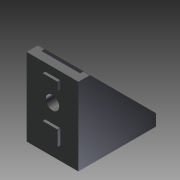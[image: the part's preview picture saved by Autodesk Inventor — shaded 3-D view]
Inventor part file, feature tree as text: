
AUTODESK INVENTOR PART (.ipt)
format: ipt  version: 2016 (Build 200138000, 138)  size: 183,808 bytes
history: native  units: mm
features: other x42, sketch x8, extrude x5, hole x3
ambient origin geometry x8: Origin, YZ Plane, XZ Plane, XY Plane, X Axis, Y Axis, Z Axis, Center Point
bodies: Solid1 (feature_tree)
feature tree (58):
  extrude  "Extrusion1"  Depth=15.0mm TaperAngle=0.0deg
  extrude  "Extrusion2"  Depth=1.0mm TaperAngle=0.0deg
  extrude  "Extrusion3"  TaperAngle=0.0deg  [1 undecoded]
  hole  "Hole1"  [1 undecoded]
  hole  "Hole2"  [1 undecoded]
  hole  "Hole3"  [1 undecoded]
  extrude  "Extrusion4"  [1 undecoded]
  extrude  "Extrusion5"  [1 undecoded]
  other  "bracket_to_bolt_XY"
  other  "bracket_to_bolt_YZ"
  other  "bracket_to_bolt_ZX"
  other  "bracket_to_bolt_X"
  other  "bracket_to_bolt_Y"
  other  "bracket_to_bolt_Z"
  other  "bracket_to_bolt_Center"
  other  "bracket_to_dummy_XY"
  other  "bracket_to_dummy_YZ"
  other  "bracket_to_dummy_ZX"
  other  "bracket_to_dummy_X"
  other  "bracket_to_dummy_Y"
  other  "bracket_to_dummy_Z"
  other  "bracket_to_dummy_Center"
  other  "to_bolt_4_7_base_XY"
  other  "to_bolt_4_7_base_YZ"
  other  "to_bolt_4_7_base_ZX"
  other  "to_bolt_4_7_base_X"
  other  "to_bolt_4_7_base_Y"
  other  "to_bolt_4_7_base_Z"
  other  "to_bolt_4_7_base_Center"
  other  "to_bolt_row_4_to_7_XY"
  other  "to_bolt_row_4_to_7_YZ"
  other  "to_bolt_row_4_to_7_ZX"
  other  "to_bolt_row_4_to_7_X"
  other  "to_bolt_row_4_to_7_Y"
  other  "to_bolt_row_4_to_7_Z"
  other  "to_bolt_row_4_to_7_Center"
  other  "to_nut_base_4_7_XY"
  other  "to_nut_base_4_7_YZ"
  other  "to_nut_base_4_7_ZX"
  other  "to_nut_base_4_7_X"
  other  "to_nut_base_4_7_Y"
  other  "to_nut_base_4_7_Z"
  other  "to_nut_base_4_7_Center"
  other  "to_nut_row_4_to_7_XY"
  other  "to_nut_row_4_to_7_YZ"
  other  "to_nut_row_4_to_7_ZX"
  other  "to_nut_row_4_to_7_X"
  other  "to_nut_row_4_to_7_Y"
  other  "to_nut_row_4_to_7_Z"
  other  "to_nut_row_4_to_7_Center"
  sketch  "Sketch_15"  dims[d29=1.0mm d30=0.0mm d31=0.0mm d32=0.0mm]
  sketch  "Sketch_16"
  sketch  "Sketch_17"
  sketch  "Sketch4"  dims[d4=2.25mm d5=0.0mm]
  sketch  "Sketch5"  dims[d13=5.2mm d14=6.0mm d15=4.0mm d16=2.0mm d17=90.0deg d18=4.5mm d19=0.0mm]
  sketch  "Sketch6"  dims[d20=5.2mm d21=6.0mm d22=4.0mm d23=2.0mm d24=90.0deg d25=4.5mm d26=0.0mm d27=1.0mm d28=0.0mm]
  sketch  "Sketch_1"  dims[d0=20.0mm d1=0.0mm d2=15.0mm d3=0.0mm]
  sketch  "Sketch_4"  dims[d6=5.2mm d7=6.0mm d8=4.0mm d9=2.0mm d10=90.0deg d11=4.5mm d12=0.0mm]
note: 6 required parameter values undecoded (feature->parameter linkage not recoverable at this tier; creation-order binding heuristic only, values carry confidence <= 0.55)
